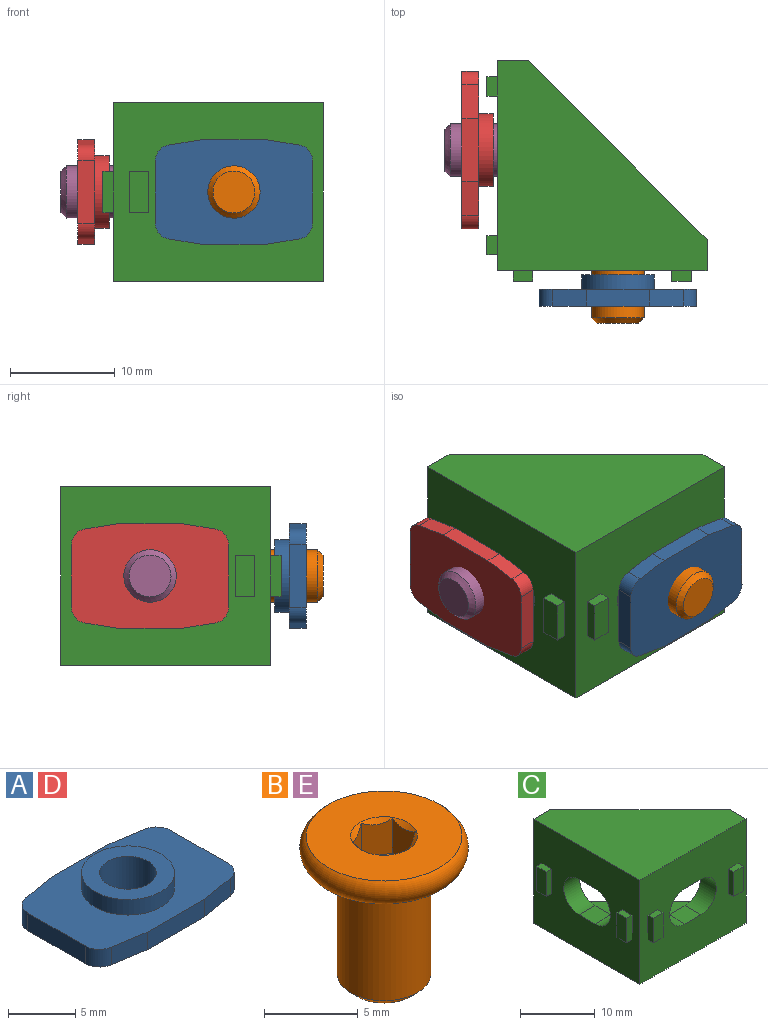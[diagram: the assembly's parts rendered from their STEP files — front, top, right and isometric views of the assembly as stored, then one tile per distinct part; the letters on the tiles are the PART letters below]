
ASSEMBLY  parts=5 mates=4
PART A: 17 faces, bbox 15x10x3 mm
  f0: cylinder r=2.1mm len=4.2mm, axis (0,0,1), area 39.6mm2, adj f15,f16
  f1: cylinder r=3.45mm len=6.9mm, axis (0,0,-1), area 30.3mm2, adj f2,f16
  f2: plane 15x10mm, normal (0,0,1), area 104.8mm2, adj f1,f3,f4,f5,f6,f7,f8,f9
  f3: cylinder r=1.5mm len=1.6mm, axis (0,0,-1), area 3.4mm2, adj f2,f4,f14,f15
  f4: plane 3.24x1.6mm, normal (0.16,0.99,0), area 5.2mm2, adj f2,f3,f5,f15
  f5: plane 6x1.6mm, normal (0,1,0), area 9.6mm2, adj f2,f4,f6,f15
  f6: plane 3.24x1.6mm, normal (-0.16,0.99,0), area 5.2mm2, adj f2,f5,f7,f15
  f7: cylinder r=1.5mm len=1.6mm, axis (0,0,-1), area 3.4mm2, adj f2,f6,f8,f15
  f8: plane 6x1.6mm, normal (-1,0,0), area 9.6mm2, adj f2,f7,f9,f15
  f9: cylinder r=1.5mm len=1.6mm, axis (0,0,-1), area 3.4mm2, adj f2,f8,f10,f15
  f10: plane 3.24x1.6mm, normal (-0.16,-0.99,0), area 5.2mm2, adj f2,f9,f11,f15
  f11: plane 6x1.6mm, normal (0,-1,0), area 9.6mm2, adj f2,f10,f12,f15
  f12: plane 3.24x1.6mm, normal (0.16,-0.99,0), area 5.2mm2, adj f2,f11,f13,f15
  f13: cylinder r=1.5mm len=1.6mm, axis (0,0,-1), area 3.4mm2, adj f2,f12,f14,f15
  f14: plane 6x1.6mm, normal (1,0,0), area 9.6mm2, adj f2,f3,f13,f15
  f15: plane 15x10mm, normal (0,0,-1), area 128.3mm2, adj f0,f3,f4,f5,f6,f7,f8,f9
  f16: plane 6.9x6.9mm, normal (0,0,1), area 23.5mm2, adj f0,f1
PART B: 14 faces, bbox 9.9x9.9x9.9 mm
  f0: cone r=1.78mm half-angle=45deg, axis (0,0,1), area 3mm2, adj f3,f7,f8,f9,f10,f11,f12
  f1: plane 8.32x8.32mm, normal (0,0,-1), area 34.8mm2, adj f2,f6
  f2: torus R=3.5mm, axis (0,0,1), area 46.7mm2, adj f1,f3
  f3: plane 8.32x8.32mm, normal (0,0,1), area 44.4mm2, adj f0,f2
  f4: plane 4x4mm, normal (0,0,-1), area 12.6mm2, adj f5
  f5: cone r=2mm half-angle=45deg, axis (0,0,1), area 10mm2, adj f4,f6
  f6: cylinder r=2.5mm len=7.5mm, axis (0,0,1), area 117.8mm2, adj f1,f5
  f7: plane 2.25x1.5mm, normal (-0.5,-0.87,0), area 3.6mm2, adj f0,f8,f12,f13
  f8: plane 2.25x1.5mm, normal (0.5,-0.87,0), area 3.6mm2, adj f0,f7,f9,f13
  f9: plane 2.25x1.73mm, normal (1,0,0), area 3.6mm2, adj f0,f8,f10,f13
  f10: plane 2.25x1.5mm, normal (0.5,0.87,0), area 3.6mm2, adj f0,f9,f11,f13
  f11: plane 2.25x1.5mm, normal (-0.5,0.87,0), area 3.6mm2, adj f0,f10,f12,f13
  f12: plane 2.42x1.9mm, normal (-1,0,0), area 3.6mm2, adj f0,f7,f11,f13
  f13: plane 3.46x3mm, normal (0,0,1), area 7.8mm2, adj f7,f8,f9,f10,f11,f12
PART C: 40 faces, bbox 21x21x17 mm
  f0: cylinder r=2.9mm len=5.8mm, axis (0,1,0), area 27.3mm2, adj f2,f13,f18,f19
  f1: cylinder r=2.9mm len=5.8mm, axis (1,0,0), area 27.3mm2, adj f3,f12,f15,f16
  f2: plane 20x17mm, normal (0,-1,0), area 281.4mm2, adj f0,f3,f6,f8,f9,f17,f18,f19
  f3: plane 20x17mm, normal (-1,0,0), area 281.4mm2, adj f1,f2,f5,f8,f9,f14,f15,f16
  f4: plane 17x17mm, normal (0.71,0.71,0), area 48.1mm2, adj f5,f6,f9,f10
  f5: plane 17x3mm, normal (0,1,0), area 51mm2, adj f3,f4,f7,f8,f9,f12
  f6: plane 17x3mm, normal (1,0,0), area 51mm2, adj f2,f4,f7,f8,f9,f13
  f7: plane 17x17mm, normal (0.71,0.71,0), area 48.1mm2, adj f5,f6,f8,f11
  f8: plane 20x20mm, normal (0,0,1), area 255.5mm2, adj f2,f3,f5,f6,f7
  f9: plane 20x20mm, normal (0,0,-1), area 255.5mm2, adj f2,f3,f4,f5,f6
  f10: plane 17x17mm, normal (0,0,1), area 144.5mm2, adj f4,f12,f13
  f11: plane 17x17mm, normal (0,0,-1), area 144.5mm2, adj f7,f12,f13
  f12: plane 17x13mm, normal (1,0,0), area 177.2mm2, adj f1,f5,f10,f11,f13,f14,f15,f16
  f13: plane 17x13mm, normal (0,1,0), area 177.2mm2, adj f0,f6,f10,f11,f12,f17,f18,f19
  f14: cylinder r=2.9mm len=5.8mm, axis (1,0,0), area 27.3mm2, adj f3,f12,f15,f16
  f15: plane 3x3mm, normal (0,0,-1), area 9mm2, adj f1,f3,f12,f14
  f16: plane 3x3mm, normal (0,0,1), area 9mm2, adj f1,f3,f12,f14
  f17: cylinder r=2.9mm len=5.8mm, axis (0,1,0), area 27.3mm2, adj f2,f13,f18,f19
  f18: plane 3x3mm, normal (0,0,-1), area 9mm2, adj f0,f2,f13,f17
  f19: plane 3x3mm, normal (0,0,1), area 9mm2, adj f0,f2,f13,f17
  f20: plane 4x1mm, normal (0,1,0), area 4mm2, adj f3,f21,f23,f24
  f21: plane 4x1.85mm, normal (-1,0,0), area 7.4mm2, adj f20,f22,f23,f24
  f22: plane 4x1mm, normal (0,-1,0), area 4mm2, adj f3,f21,f23,f24
  f23: plane 1.85x1mm, normal (0,0,1), area 1.9mm2, adj f3,f20,f21,f22
  f24: plane 1.85x1mm, normal (0,0,-1), area 1.9mm2, adj f3,f20,f21,f22
  f25: plane 4x1mm, normal (0,-1,0), area 4mm2, adj f3,f27,f28,f29
  f26: plane 4x1mm, normal (0,1,0), area 4mm2, adj f3,f27,f28,f29
  f27: plane 4x1.85mm, normal (-1,0,0), area 7.4mm2, adj f25,f26,f28,f29
  f28: plane 1.85x1mm, normal (0,0,1), area 1.9mm2, adj f3,f25,f26,f27
  f29: plane 1.85x1mm, normal (0,0,-1), area 1.9mm2, adj f3,f25,f26,f27
  f30: plane 4x1mm, normal (-1,0,0), area 4mm2, adj f2,f31,f33,f34
  f31: plane 4x1.85mm, normal (0,-1,0), area 7.4mm2, adj f30,f32,f33,f34
  f32: plane 4x1mm, normal (1,0,0), area 4mm2, adj f2,f31,f33,f34
  f33: plane 1.85x1mm, normal (0,0,1), area 1.9mm2, adj f2,f30,f31,f32
  f34: plane 1.85x1mm, normal (0,0,-1), area 1.9mm2, adj f2,f30,f31,f32
  f35: plane 4x1mm, normal (1,0,0), area 4mm2, adj f2,f37,f38,f39
  f36: plane 4x1mm, normal (-1,0,0), area 4mm2, adj f2,f37,f38,f39
  f37: plane 4x1.85mm, normal (0,-1,0), area 7.4mm2, adj f35,f36,f38,f39
  f38: plane 1.85x1mm, normal (0,0,1), area 1.9mm2, adj f2,f35,f36,f37
  f39: plane 1.85x1mm, normal (0,0,-1), area 1.9mm2, adj f2,f35,f36,f37
PART D: same geometry as A
PART E: same geometry as B
PLACE A rot(axis=(-1,0,0),90deg) t=(-0.12,-43.47,72.61)mm
PLACE B rot(axis=(-1,0,0),90deg) t=(14.88,-37.07,72.61)mm
PLACE C t=(-11.62,-40.07,72.61)mm
PLACE D rot(axis=(0.58,0.58,0.58),120deg) t=(-15.02,-28.57,72.61)mm
PLACE E rot(axis=(0.71,0,0.71),180deg) t=(-8.62,-28.57,87.61)mm
MATE fastened B.f2 <-> C.f17  axis (0,1,0) through (-0.12,-37.07,72.61)mm
MATE fastened E.f2 <-> C.f1  axis (1,0,0) through (-8.62,-28.57,72.61)mm
MATE fastened D.f0 <-> C.f1  axis (1,0,0) through (-13.42,-28.57,72.61)mm
MATE fastened A.f0 <-> C.f17  axis (0,1,0) through (-0.12,-41.87,72.61)mm
